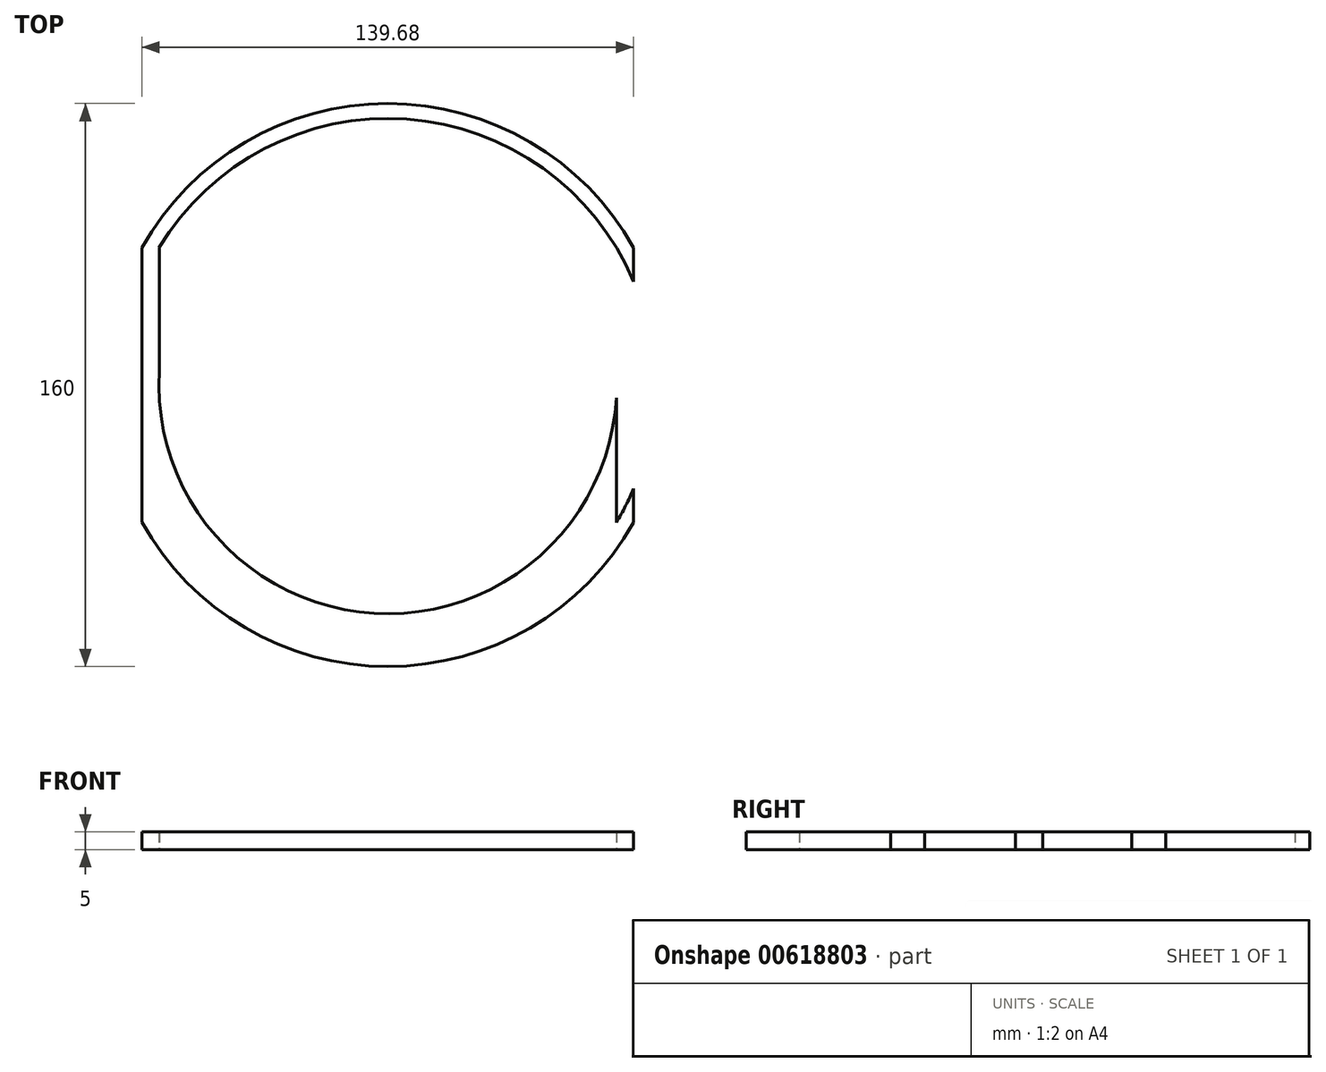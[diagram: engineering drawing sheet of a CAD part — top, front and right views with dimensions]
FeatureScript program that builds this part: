
annotation { "Feature Type Name" : "Feature", "Feature Type Description" : "" }
export const myFeature = defineFeature(function(context is Context, id is Id, definition is map)
    precondition{}
    {
        {
            var Q0;
            Q0=qCreatedBy(makeId("Top.planeOp"),FACE);
            var sketch = newSketch(context, id + "F0", { "sketchPlane" : qUnion([Q0])});
            skCircle(sketch, "E0", {"center": v(0, 0) * mm, "radius": 80 * mm});
            skCircle(sketch, "E1", {"center": v(0, 0) * mm, "radius": 75.75 * mm});
            skCircle(sketch, "E2", {"center": v(0, 0) * mm, "radius": 65 * mm});
            skLineSegment(sketch, "E3", {"start": v(-69.87, 38.96) * mm, "end": v(-69.87, -38.96) * mm});
            skLineSegment(sketch, "E4", {"start": v(69.81, 39.07) * mm, "end": v(69.81, -39.07) * mm});
            skLineSegment(sketch, "E5", {"start": v(-69.87, 38.96) * mm, "end": v(69.81, 39.07) * mm, "construction": true});
            skLineSegment(sketch, "E6", {"start": v(-69.87, -38.96) * mm, "end": v(69.81, -39.07) * mm, "construction": true});
            skLineSegment(sketch, "E7", {"start": v(-64.87, 38.97) * mm, "end": v(-64.87, -38.97) * mm});
            skLineSegment(sketch, "E8", {"start": v(-69.87, -38.96) * mm, "end": v(-64.87, -38.97) * mm});
            skLineSegment(sketch, "E9", {"start": v(-69.87, 38.96) * mm, "end": v(-64.87, 38.97) * mm});
            skLineSegment(sketch, "E10", {"start": v(69.81, 39.07) * mm, "end": v(64.9, 39.07) * mm});
            skLineSegment(sketch, "E11", {"start": v(64.9, 39.07) * mm, "end": v(64.9, -39.07) * mm});
            skLineSegment(sketch, "E12", {"start": v(64.9, -39.07) * mm, "end": v(69.81, -39.07) * mm});
            skSolve(sketch);
        }
        {
            var Q0;
            {var subQ3=sQuery(id+"F0.wireOp",EDGE,"E10");Q0=makeQuery(id+"F0.imprint","IMPRINT",FACE,{"disambiguationData":[TD([[makeQuery(id+"F0.imprint","IMPRINT",EDGE,{"derivedFrom":subQ3}),-1.0]])]});}
            var Q1;
            {var subQ1=sQuery(id+"F0.wireOp",EDGE,"E1");var subQ4=sQuery(id+"F0.wireOp",EDGE,"E9");var subQ5=makeQuery(id+"F0.imprint","INTERSECT",VERTEX,{"derivedFrom":[subQ1,subQ4]});Q1=makeQuery(id+"F0.imprint","IMPRINT",FACE,{"disambiguationData":[TD([[makeQuery(id+"F0.imprint","IMPRINT",EDGE,{"disambiguationData":[TD([[subQ5,-1.0]])],"derivedFrom":subQ1}),1.0]])]});}
            var Q2;
            {var subQ0=sQuery(id+"F0.wireOp",EDGE,"E9");var subQ1=sQuery(id+"F0.wireOp",EDGE,"E1");var subQ2=makeQuery(id+"F0.imprint","INTERSECT",VERTEX,{"derivedFrom":[subQ1,subQ0]});Q2=makeQuery(id+"F0.imprint","IMPRINT",FACE,{"disambiguationData":[TD([[makeQuery(id+"F0.imprint","IMPRINT",EDGE,{"disambiguationData":[TD([[subQ2,-1.0]])],"derivedFrom":subQ1}),-1.0]])]});}
            var Q3;
            {var subQ0=sQuery(id+"F0.wireOp",EDGE,"E3");var subQ1=sQuery(id+"F0.wireOp",EDGE,"E1");var subQ2=makeQuery(id+"F0.imprint","INTERSECT",VERTEX,{"disambiguationData":[OD(1.0)],"derivedFrom":[subQ1,subQ0]});Q3=makeQuery(id+"F0.imprint","IMPRINT",FACE,{"disambiguationData":[TD([[makeQuery(id+"F0.imprint","IMPRINT",EDGE,{"disambiguationData":[TD([[subQ2,-1.0]])],"derivedFrom":subQ1}),-1.0]])]});}
            var Q4;
            {var subQ3=sQuery(id+"F0.wireOp",EDGE,"E12");Q4=makeQuery(id+"F0.imprint","IMPRINT",FACE,{"disambiguationData":[TD([[makeQuery(id+"F0.imprint","IMPRINT",EDGE,{"derivedFrom":subQ3}),-1.0]])]});}
            var Q5;
            {var subQ4=sQuery(id+"F0.wireOp",EDGE,"E11");var subQ5=sQuery(id+"F0.wireOp",EDGE,"E2");var subQ6=makeQuery(id+"F0.imprint","INTERSECT",VERTEX,{"disambiguationData":[OD(0.0)],"derivedFrom":[subQ5,subQ4]});Q5=makeQuery(id+"F0.imprint","IMPRINT",FACE,{"disambiguationData":[TD([[makeQuery(id+"F0.imprint","IMPRINT",EDGE,{"disambiguationData":[TD([[subQ6,1.0]])],"derivedFrom":subQ5}),-1.0]])]});}
            var Q6;
            {var subQ0=sQuery(id+"F0.wireOp",EDGE,"E12");Q6=makeQuery(id+"F0.imprint","IMPRINT",FACE,{"disambiguationData":[TD([[makeQuery(id+"F0.imprint","IMPRINT",EDGE,{"derivedFrom":subQ0}),1.0]])]});}
            var Q7;
            {var subQ0=sQuery(id+"F0.wireOp",EDGE,"E10");Q7=makeQuery(id+"F0.imprint","IMPRINT",FACE,{"disambiguationData":[TD([[makeQuery(id+"F0.imprint","IMPRINT",EDGE,{"derivedFrom":subQ0}),1.0]])]});}
            extrude(context, id + "F1", {"entities" : qUnion([Q0, Q1, Q2, Q3, Q4, Q5, Q6, Q7]), "depth" : 5 * mm, "offsetDistance" : 25 * mm});
        }
        {
            var Q0;
            {var subQ1=sQuery(id+"F0.wireOp",EDGE,"E7");var subQ5=sQuery(id+"F0.wireOp",EDGE,"E2");var subQ6=makeQuery(id+"F0.imprint","INTERSECT",VERTEX,{"disambiguationData":[OD(1.0)],"derivedFrom":[subQ5,subQ1]});Q0=makeQuery(id+"F0.imprint","IMPRINT",FACE,{"disambiguationData":[TD([[makeQuery(id+"F0.imprint","IMPRINT",EDGE,{"disambiguationData":[TD([[subQ6,-1.0]])],"derivedFrom":subQ5}),-1.0]])]});}
            var Q1;
            {var subQ1=sQuery(id+"F0.wireOp",EDGE,"E7");var subQ5=sQuery(id+"F0.wireOp",EDGE,"E2");var subQ6=makeQuery(id+"F0.imprint","INTERSECT",VERTEX,{"disambiguationData":[OD(0.0)],"derivedFrom":[subQ5,subQ1]});Q1=makeQuery(id+"F0.imprint","IMPRINT",FACE,{"disambiguationData":[TD([[makeQuery(id+"F0.imprint","IMPRINT",EDGE,{"disambiguationData":[TD([[subQ6,1.0]])],"derivedFrom":subQ5}),-1.0]])]});}
            extrude(context, id + "F2", {"entities" : qUnion([Q0, Q1]), "operationType" : NewBodyOperationType.ADD, "depth" : 3 * mm, "offsetDistance" : 25 * mm});
        }
    });
